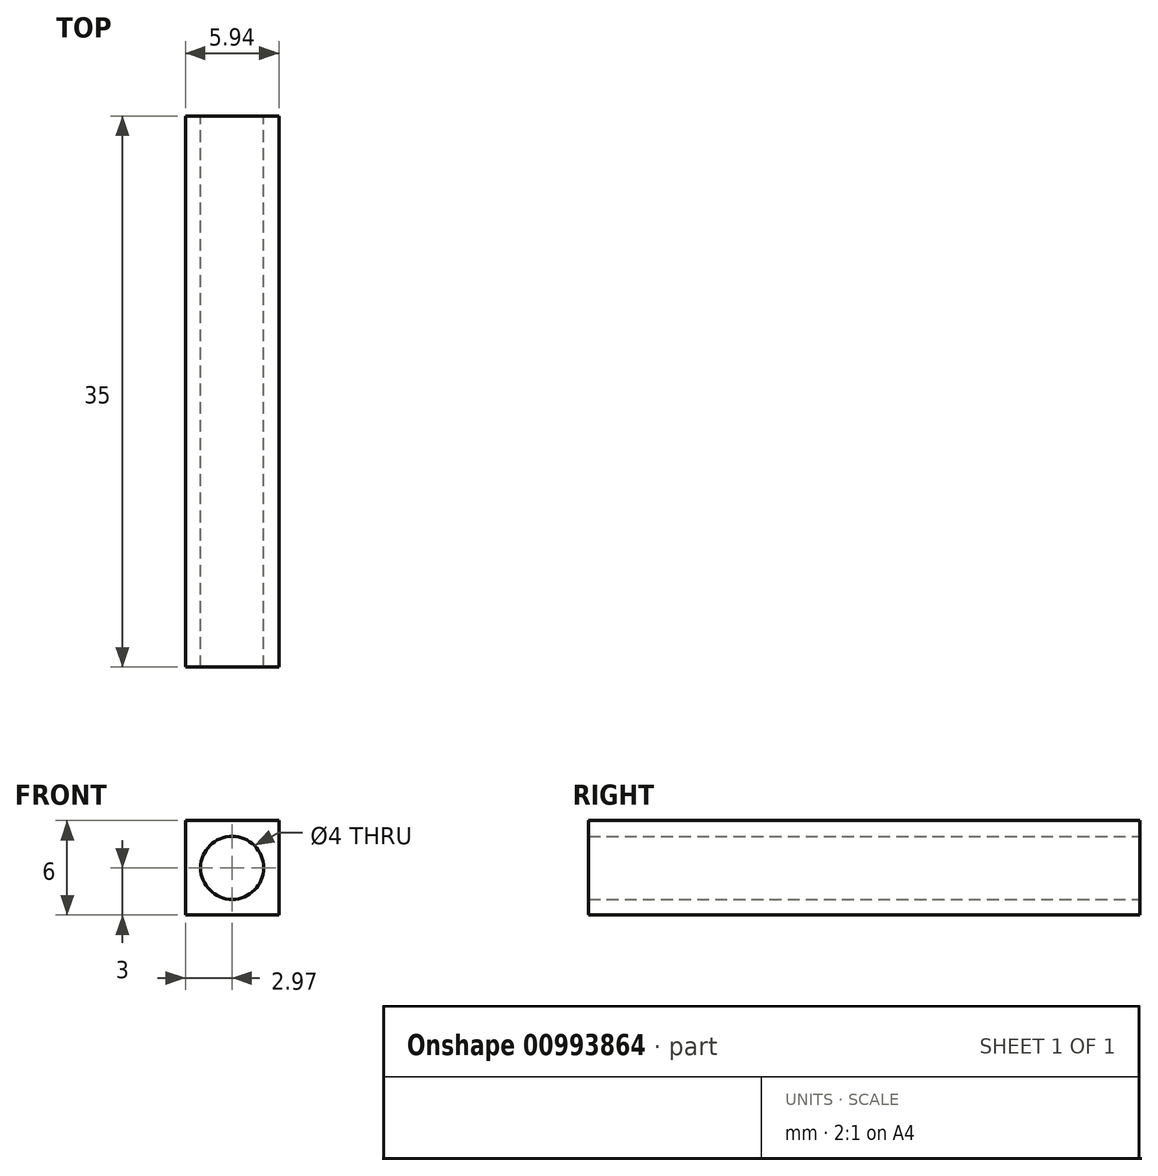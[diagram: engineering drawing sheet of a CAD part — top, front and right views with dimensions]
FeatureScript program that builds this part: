
annotation { "Feature Type Name" : "Feature", "Feature Type Description" : "" }
export const myFeature = defineFeature(function(context is Context, id is Id, definition is map)
    precondition{}
    {
        {
            var Q0;
            Q0=qCreatedBy(makeId("Front.planeOp"),FACE);
            var sketch = newSketch(context, id + "F0", { "sketchPlane" : qUnion([Q0])});
            skCircle(sketch, "E0", {"center": v(0, 0) * mm, "radius": 2 * mm});
            skLineSegment(sketch, "E1.bottom", {"start": v(2.97, -3) * mm, "end": v(-2.97, -3) * mm});
            skLineSegment(sketch, "E1.top", {"start": v(2.97, 3) * mm, "end": v(-2.97, 3) * mm});
            skLineSegment(sketch, "E1.left", {"start": v(2.97, -3) * mm, "end": v(2.97, 3) * mm});
            skLineSegment(sketch, "E1.right", {"start": v(-2.97, -3) * mm, "end": v(-2.97, 3) * mm});
            skSolve(sketch);
        }
        {
            var Q0;
            Q0=makeQuery(id+"F0.imprint","IMPRINT",FACE,{"disambiguationData":[TD([[makeQuery(id+"F0.imprint","IMPRINT",EDGE,{"derivedFrom":sQuery(id+"F0.wireOp",EDGE,"E0")}),-1.0]])]});
            extrude(context, id + "F1", {"entities" : qUnion([Q0]), "depth" : 10 * mm, "offsetDistance" : 25 * mm});
        }
        {
            var Q0;
            Q0=makeQuery(id+"F1.opExtrude","CAP_FACE",FACE,{"disambiguationData":[OSD([sQuery(id+"F0.wireOp",EDGE,"E0"),sQuery(id+"F0.wireOp",EDGE,"E1.bottom"),sQuery(id+"F0.wireOp",EDGE,"E1.top"),sQuery(id+"F0.wireOp",EDGE,"E1.left"),sQuery(id+"F0.wireOp",EDGE,"E1.right")])],"isStart":false});
            extrude(context, id + "F2", {"entities" : qUnion([Q0]), "operationType" : NewBodyOperationType.ADD, "depth" : 25 * mm, "offsetDistance" : 25 * mm});
        }
    });
